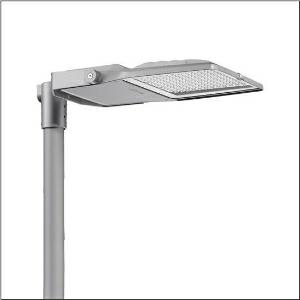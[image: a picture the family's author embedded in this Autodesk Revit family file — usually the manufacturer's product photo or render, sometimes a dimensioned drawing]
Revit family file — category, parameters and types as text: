
# Revit family: floodlight_fl_21_midi___pl64_5xa7785e2e3a_0c5c
name_source: partatom
category: Lighting Fixtures
units: mm (PartAtom-declared; Revit-internal decimal feet)

## family parameters
Cut with Voids When Loaded = No
Host = Face
Light Source = No
Part Type = Normal
Room Calculation Point = No
Round Connector Dimension = Use Diameter
Shared = No

## types (1)
- --- (1 x LED, 26020 lm, 212.4 W, 3000K)
    Apparent Load = 212 VA
    CIE Flux Codes = 28 80 98 100 100
    Color Rendering = 70
    Color Temperature = 3000K
    Default Elevation = 1800 mm
    Description = Floodlight FL 21 midi, floodlight, primary light control with lens, of PMMA, primary optical cover: protective disc, of toughened safety glass, transparent, light distribution: PL64, light emission: direct distribution, installation type: surface-mounted, LED, High Power LED, rated luminous flux: 26.020lm, luminous efficacy: 123lm/W, light colour: 730, colour temperature: 3000K, control gear: Smart Interface (Zhaga), control: flexible luminous flux parameterisation, time-dependent luminous flux control, constant luminous flux control, overheat protection, pre-setting: logarithmic dimming characteristic, with terminal, 6-pole, mains connection: 220..240V, AC, 50/60Hz, start of lifetime: 212W, end of service life: 231W, reduction: 95W, luminaire housing, of diecast aluminium, powder-coated, SITECO metallic grey (DB 702S), corrosivity category C5 mid according to DIN EN ISO 12944, suitable for swimming pools, chlorine-resistant, sealing non-destructively replaceable, please order mast flange separately, mast bracket, of steel, galvanised, powder-coated, SITECO metallic grey (DB 702S), Smart Interface above, protection rating (complete): IP66, insulation class (complete): insulation class II (safety insulation), certification: CE, ENEC, VDE, protection symbol: D, impact resistance: IK08, permissible operating ambient temperature: -20..+40°C, permissible operating ambient temperature for outdoor applications: -40..+50°C, standard: DIN EN 12944, LABS conformity tested according to VDMA 24364:2018-05, packaging unit: 1 piece

Light Distribution: PL64
    Height = 76 mm
    Lamp = 1 x LED
    Lamp Light Flux = 26020 lm
    Lamp Power = 212.4 W
    Lamp count = 1
    Length = 657 mm
    Luminous efficacy = 123 lm/W
    Manufacturer = Siteco
    ModVariant = No
    Model = 5XA7785E2E3A
    Number of Poles = 1
    OnlyDefault = Yes
    Power Factor = 1
    Product Name = Floodlight FL 21 midi | PL64
    Product group = floodlight | pylon annexe
    ProductGroupID = 6201
    Protection Class = Protection class II
    Protection Degree = IP 66
    RLX_Detail_Level = 1
    RLX_Emergency_Light_Flux = 0 lm
    RLX_Emergency_Type = 0
    RLX_Emergency_Type_DB = No
    RlxData = <blob elided: 153733 chars, md5=609df5b0>
    Socket = socket
    Standby Power = 0 W
    System Light Flux = 26020 lm
    System Power = 212 W
    Type Comments = factory setting: luminous flux: 100 % | dim-lin: 254 | 710 mA
    Type Image = l_1007123.jpg
    URL = http://relux.com
    VarID = @adj_179161
    Voltage = 0 V
    Weight = 0.00 kg
    Width = 442 mm

## geometry (parser evidence)
native form markers: Blend x4, Sweep x13
no freeform markers — native parametric forms only
